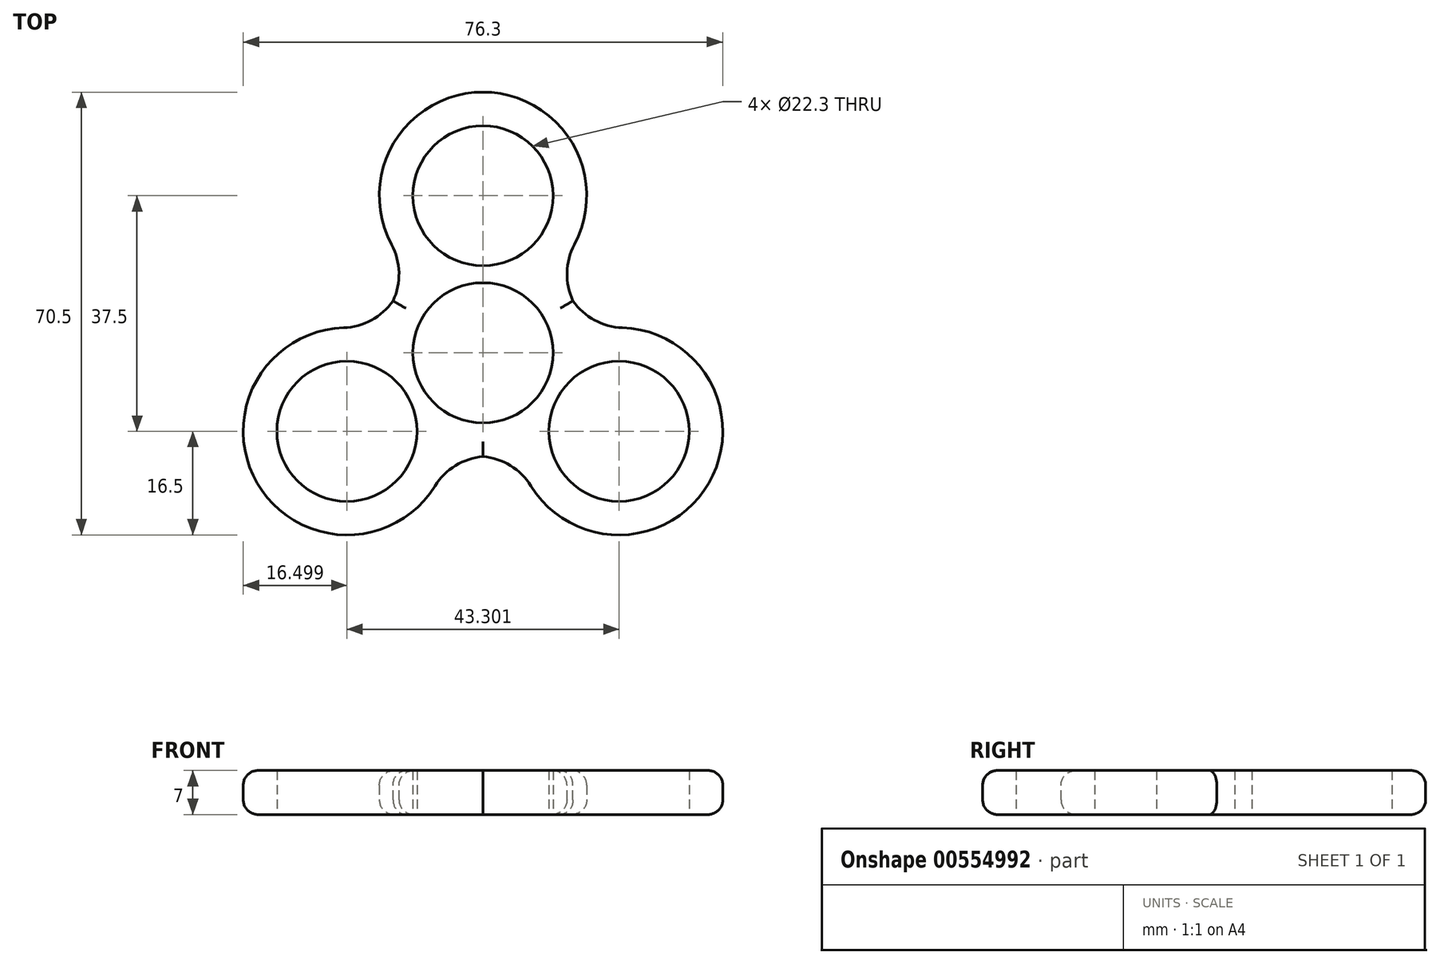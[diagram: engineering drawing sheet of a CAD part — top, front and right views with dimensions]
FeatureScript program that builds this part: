
annotation { "Feature Type Name" : "Feature", "Feature Type Description" : "" }
export const myFeature = defineFeature(function(context is Context, id is Id, definition is map)
    precondition{}
    {
        {
            var Q0;
            Q0=qCreatedBy(makeId("Top.planeOp"),FACE);
            var sketch = newSketch(context, id + "F0", { "sketchPlane" : qUnion([Q0])});
            skCircle(sketch, "E0", {"center": v(0, 0) * mm, "radius": 11.15 * mm});
            skLineSegment(sketch, "E1", {"start": v(0, 0) * mm, "end": v(0, 25) * mm, "construction": true});
            skCircle(sketch, "E2", {"center": v(0, 25) * mm, "radius": 11.15 * mm});
            skCircle(sketch, "E3.1.0", {"center": v(-21.65, -12.5) * mm, "radius": 11.15 * mm});
            skCircle(sketch, "E3.2.0", {"center": v(21.65, -12.5) * mm, "radius": 11.15 * mm});
            skCircle(sketch, "E4", {"center": v(0, 25) * mm, "radius": 16.5 * mm});
            skCircle(sketch, "E5", {"center": v(21.65, -12.5) * mm, "radius": 16.5 * mm});
            skCircle(sketch, "E6", {"center": v(-21.65, -12.5) * mm, "radius": 16.5 * mm});
            skLineSegment(sketch, "E7", {"start": v(0, 0) * mm, "end": v(-21.65, -12.5) * mm});
            skCircle(sketch, "E8", {"center": v(0, 0) * mm, "radius": 16.5 * mm});
            skSolve(sketch);
        }
        {
            var Q0;
            Q0=qSketchRegion(id+"F0",true);
            extrude(context, id + "F1", {"entities" : qUnion([Q0]), "depth" : 7 * mm, "offsetDistance" : 25 * mm});
        }
        {
            var Q0;
            {var subQ0=sQuery(id+"F0.wireOp",EDGE,"E8");var subQ1=sQuery(id+"F0.wireOp",EDGE,"E6");Q0=makeQuery(id+"F1.opExtrude","SWEPT_EDGE",EDGE,{"disambiguationData":[OSD([subQ1,subQ0]),TDD([makeQuery(id+"F0.imprint","INTERSECT",VERTEX,{"disambiguationData":[OD(1.0)],"derivedFrom":[subQ1,subQ0]})])]});}
            var Q1;
            {var subQ0=sQuery(id+"F0.wireOp",EDGE,"E8");var subQ1=sQuery(id+"F0.wireOp",EDGE,"E4");Q1=makeQuery(id+"F1.opExtrude","SWEPT_EDGE",EDGE,{"disambiguationData":[OSD([subQ1,subQ0]),TDD([makeQuery(id+"F0.imprint","INTERSECT",VERTEX,{"disambiguationData":[OD(0.0)],"derivedFrom":[subQ1,subQ0]})])]});}
            var Q2;
            {var subQ0=sQuery(id+"F0.wireOp",EDGE,"E8");var subQ1=sQuery(id+"F0.wireOp",EDGE,"E4");Q2=makeQuery(id+"F1.opExtrude","SWEPT_EDGE",EDGE,{"disambiguationData":[OSD([subQ1,subQ0]),TDD([makeQuery(id+"F0.imprint","INTERSECT",VERTEX,{"disambiguationData":[OD(1.0)],"derivedFrom":[subQ1,subQ0]})])]});}
            var Q3;
            {var subQ0=sQuery(id+"F0.wireOp",EDGE,"E8");var subQ1=sQuery(id+"F0.wireOp",EDGE,"E5");Q3=makeQuery(id+"F1.opExtrude","SWEPT_EDGE",EDGE,{"disambiguationData":[OSD([subQ1,subQ0]),TDD([makeQuery(id+"F0.imprint","INTERSECT",VERTEX,{"disambiguationData":[OD(1.0)],"derivedFrom":[subQ1,subQ0]})])]});}
            var Q4;
            {var subQ0=sQuery(id+"F0.wireOp",EDGE,"E8");var subQ1=sQuery(id+"F0.wireOp",EDGE,"E5");Q4=makeQuery(id+"F1.opExtrude","SWEPT_EDGE",EDGE,{"disambiguationData":[OSD([subQ1,subQ0]),TDD([makeQuery(id+"F0.imprint","INTERSECT",VERTEX,{"disambiguationData":[OD(0.0)],"derivedFrom":[subQ1,subQ0]})])]});}
            var Q5;
            {var subQ0=sQuery(id+"F0.wireOp",EDGE,"E8");var subQ1=sQuery(id+"F0.wireOp",EDGE,"E6");Q5=makeQuery(id+"F1.opExtrude","SWEPT_EDGE",EDGE,{"disambiguationData":[OSD([subQ1,subQ0]),TDD([makeQuery(id+"F0.imprint","INTERSECT",VERTEX,{"disambiguationData":[OD(0.0)],"derivedFrom":[subQ1,subQ0]})])]});}
            fillet(context, id + "F2", {"entities" : qUnion([Q0, Q1, Q2, Q3, Q4, Q5]), "radius" : 10 * mm, "tangentPropagation" : true, "allowEdgeOverflow" : false});
        }
        {
            var Q0;
            Q0=makeQuery(id+"F1.opExtrude","CAP_EDGE",EDGE,{"disambiguationData":[OSD([sQuery(id+"F0.wireOp",EDGE,"E4")])],"isStart":false});
            var Q1;
            {var subQ0=sQuery(id+"F0.wireOp",EDGE,"E8");var subQ1=sQuery(id+"F0.wireOp",EDGE,"E4");Q1=makeQuery(id+"F2.opFillet","BLEND_EDGE",EDGE,{"blendedFrom":[makeQuery(id+"F1.opExtrude","SWEPT_EDGE",EDGE,{"disambiguationData":[OSD([subQ1,subQ0]),TDD([makeQuery(id+"F0.imprint","INTERSECT",VERTEX,{"disambiguationData":[OD(0.0)],"derivedFrom":[subQ1,subQ0]})])]}),makeQuery(id+"F1.opExtrude","CAP_FACE",FACE,{"disambiguationData":[OSD([sQuery(id+"F0.wireOp",EDGE,"E0"),sQuery(id+"F0.wireOp",EDGE,"E2"),sQuery(id+"F0.wireOp",EDGE,"E3.1.0"),sQuery(id+"F0.wireOp",EDGE,"E3.2.0"),subQ1,sQuery(id+"F0.wireOp",EDGE,"E5"),sQuery(id+"F0.wireOp",EDGE,"E6"),subQ0])],"isStart":false})],"blendedInto":[makeQuery(id+"F1.opExtrude","CAP_FACE",FACE,{"disambiguationData":[OSD([sQuery(id+"F0.wireOp",EDGE,"E0"),sQuery(id+"F0.wireOp",EDGE,"E2"),sQuery(id+"F0.wireOp",EDGE,"E3.1.0"),sQuery(id+"F0.wireOp",EDGE,"E3.2.0"),subQ1,sQuery(id+"F0.wireOp",EDGE,"E5"),sQuery(id+"F0.wireOp",EDGE,"E6"),subQ0])],"isStart":false})]});}
            var Q2;
            {var subQ0=sQuery(id+"F0.wireOp",EDGE,"E8");var subQ1=sQuery(id+"F0.wireOp",EDGE,"E6");Q2=makeQuery(id+"F2.opFillet","BLEND_EDGE",EDGE,{"blendedFrom":[makeQuery(id+"F1.opExtrude","SWEPT_EDGE",EDGE,{"disambiguationData":[OSD([subQ1,subQ0]),TDD([makeQuery(id+"F0.imprint","INTERSECT",VERTEX,{"disambiguationData":[OD(1.0)],"derivedFrom":[subQ1,subQ0]})])]}),makeQuery(id+"F1.opExtrude","CAP_FACE",FACE,{"disambiguationData":[OSD([sQuery(id+"F0.wireOp",EDGE,"E0"),sQuery(id+"F0.wireOp",EDGE,"E2"),sQuery(id+"F0.wireOp",EDGE,"E3.1.0"),sQuery(id+"F0.wireOp",EDGE,"E3.2.0"),sQuery(id+"F0.wireOp",EDGE,"E4"),sQuery(id+"F0.wireOp",EDGE,"E5"),subQ1,subQ0])],"isStart":false})],"blendedInto":[makeQuery(id+"F1.opExtrude","CAP_FACE",FACE,{"disambiguationData":[OSD([sQuery(id+"F0.wireOp",EDGE,"E0"),sQuery(id+"F0.wireOp",EDGE,"E2"),sQuery(id+"F0.wireOp",EDGE,"E3.1.0"),sQuery(id+"F0.wireOp",EDGE,"E3.2.0"),sQuery(id+"F0.wireOp",EDGE,"E4"),sQuery(id+"F0.wireOp",EDGE,"E5"),subQ1,subQ0])],"isStart":false})]});}
            var Q3;
            Q3=makeQuery(id+"F1.opExtrude","CAP_EDGE",EDGE,{"disambiguationData":[OSD([sQuery(id+"F0.wireOp",EDGE,"E6")])],"isStart":false});
            var Q4;
            {var subQ0=sQuery(id+"F0.wireOp",EDGE,"E8");var subQ1=sQuery(id+"F0.wireOp",EDGE,"E5");Q4=makeQuery(id+"F2.opFillet","BLEND_EDGE",EDGE,{"blendedFrom":[makeQuery(id+"F1.opExtrude","SWEPT_EDGE",EDGE,{"disambiguationData":[OSD([subQ1,subQ0]),TDD([makeQuery(id+"F0.imprint","INTERSECT",VERTEX,{"disambiguationData":[OD(0.0)],"derivedFrom":[subQ1,subQ0]})])]}),makeQuery(id+"F1.opExtrude","CAP_FACE",FACE,{"disambiguationData":[OSD([sQuery(id+"F0.wireOp",EDGE,"E0"),sQuery(id+"F0.wireOp",EDGE,"E2"),sQuery(id+"F0.wireOp",EDGE,"E3.1.0"),sQuery(id+"F0.wireOp",EDGE,"E3.2.0"),sQuery(id+"F0.wireOp",EDGE,"E4"),subQ1,sQuery(id+"F0.wireOp",EDGE,"E6"),subQ0])],"isStart":false})],"blendedInto":[makeQuery(id+"F1.opExtrude","CAP_FACE",FACE,{"disambiguationData":[OSD([sQuery(id+"F0.wireOp",EDGE,"E0"),sQuery(id+"F0.wireOp",EDGE,"E2"),sQuery(id+"F0.wireOp",EDGE,"E3.1.0"),sQuery(id+"F0.wireOp",EDGE,"E3.2.0"),sQuery(id+"F0.wireOp",EDGE,"E4"),subQ1,sQuery(id+"F0.wireOp",EDGE,"E6"),subQ0])],"isStart":false})]});}
            var Q5;
            Q5=makeQuery(id+"F1.opExtrude","CAP_EDGE",EDGE,{"disambiguationData":[OSD([sQuery(id+"F0.wireOp",EDGE,"E5")])],"isStart":false});
            var Q6;
            Q6=makeQuery(id+"F1.opExtrude","CAP_EDGE",EDGE,{"disambiguationData":[OSD([sQuery(id+"F0.wireOp",EDGE,"E6")])],"isStart":true});
            var Q7;
            {var subQ0=sQuery(id+"F0.wireOp",EDGE,"E8");var subQ1=sQuery(id+"F0.wireOp",EDGE,"E6");Q7=makeQuery(id+"F2.opFillet","BLEND_EDGE",EDGE,{"blendedFrom":[makeQuery(id+"F1.opExtrude","SWEPT_EDGE",EDGE,{"disambiguationData":[OSD([subQ1,subQ0]),TDD([makeQuery(id+"F0.imprint","INTERSECT",VERTEX,{"disambiguationData":[OD(0.0)],"derivedFrom":[subQ1,subQ0]})])]}),makeQuery(id+"F1.opExtrude","CAP_FACE",FACE,{"disambiguationData":[OSD([sQuery(id+"F0.wireOp",EDGE,"E0"),sQuery(id+"F0.wireOp",EDGE,"E2"),sQuery(id+"F0.wireOp",EDGE,"E3.1.0"),sQuery(id+"F0.wireOp",EDGE,"E3.2.0"),sQuery(id+"F0.wireOp",EDGE,"E4"),sQuery(id+"F0.wireOp",EDGE,"E5"),subQ1,subQ0])],"isStart":true})],"blendedInto":[makeQuery(id+"F1.opExtrude","CAP_FACE",FACE,{"disambiguationData":[OSD([sQuery(id+"F0.wireOp",EDGE,"E0"),sQuery(id+"F0.wireOp",EDGE,"E2"),sQuery(id+"F0.wireOp",EDGE,"E3.1.0"),sQuery(id+"F0.wireOp",EDGE,"E3.2.0"),sQuery(id+"F0.wireOp",EDGE,"E4"),sQuery(id+"F0.wireOp",EDGE,"E5"),subQ1,subQ0])],"isStart":true})]});}
            var Q8;
            Q8=makeQuery(id+"F1.opExtrude","CAP_EDGE",EDGE,{"disambiguationData":[OSD([sQuery(id+"F0.wireOp",EDGE,"E5")])],"isStart":true});
            var Q9;
            {var subQ0=sQuery(id+"F0.wireOp",EDGE,"E8");var subQ1=sQuery(id+"F0.wireOp",EDGE,"E5");Q9=makeQuery(id+"F2.opFillet","BLEND_EDGE",EDGE,{"blendedFrom":[makeQuery(id+"F1.opExtrude","SWEPT_EDGE",EDGE,{"disambiguationData":[OSD([subQ1,subQ0]),TDD([makeQuery(id+"F0.imprint","INTERSECT",VERTEX,{"disambiguationData":[OD(1.0)],"derivedFrom":[subQ1,subQ0]})])]}),makeQuery(id+"F1.opExtrude","CAP_FACE",FACE,{"disambiguationData":[OSD([sQuery(id+"F0.wireOp",EDGE,"E0"),sQuery(id+"F0.wireOp",EDGE,"E2"),sQuery(id+"F0.wireOp",EDGE,"E3.1.0"),sQuery(id+"F0.wireOp",EDGE,"E3.2.0"),sQuery(id+"F0.wireOp",EDGE,"E4"),subQ1,sQuery(id+"F0.wireOp",EDGE,"E6"),subQ0])],"isStart":true})],"blendedInto":[makeQuery(id+"F1.opExtrude","CAP_FACE",FACE,{"disambiguationData":[OSD([sQuery(id+"F0.wireOp",EDGE,"E0"),sQuery(id+"F0.wireOp",EDGE,"E2"),sQuery(id+"F0.wireOp",EDGE,"E3.1.0"),sQuery(id+"F0.wireOp",EDGE,"E3.2.0"),sQuery(id+"F0.wireOp",EDGE,"E4"),subQ1,sQuery(id+"F0.wireOp",EDGE,"E6"),subQ0])],"isStart":true})]});}
            var Q10;
            {var subQ0=sQuery(id+"F0.wireOp",EDGE,"E8");var subQ1=sQuery(id+"F0.wireOp",EDGE,"E4");Q10=makeQuery(id+"F2.opFillet","BLEND_EDGE",EDGE,{"blendedFrom":[makeQuery(id+"F1.opExtrude","SWEPT_EDGE",EDGE,{"disambiguationData":[OSD([subQ1,subQ0]),TDD([makeQuery(id+"F0.imprint","INTERSECT",VERTEX,{"disambiguationData":[OD(1.0)],"derivedFrom":[subQ1,subQ0]})])]}),makeQuery(id+"F1.opExtrude","CAP_FACE",FACE,{"disambiguationData":[OSD([sQuery(id+"F0.wireOp",EDGE,"E0"),sQuery(id+"F0.wireOp",EDGE,"E2"),sQuery(id+"F0.wireOp",EDGE,"E3.1.0"),sQuery(id+"F0.wireOp",EDGE,"E3.2.0"),subQ1,sQuery(id+"F0.wireOp",EDGE,"E5"),sQuery(id+"F0.wireOp",EDGE,"E6"),subQ0])],"isStart":true})],"blendedInto":[makeQuery(id+"F1.opExtrude","CAP_FACE",FACE,{"disambiguationData":[OSD([sQuery(id+"F0.wireOp",EDGE,"E0"),sQuery(id+"F0.wireOp",EDGE,"E2"),sQuery(id+"F0.wireOp",EDGE,"E3.1.0"),sQuery(id+"F0.wireOp",EDGE,"E3.2.0"),subQ1,sQuery(id+"F0.wireOp",EDGE,"E5"),sQuery(id+"F0.wireOp",EDGE,"E6"),subQ0])],"isStart":true})]});}
            var Q11;
            Q11=makeQuery(id+"F1.opExtrude","CAP_EDGE",EDGE,{"disambiguationData":[OSD([sQuery(id+"F0.wireOp",EDGE,"E4")])],"isStart":true});
            fillet(context, id + "F3", {"entities" : qUnion([Q0, Q1, Q2, Q3, Q4, Q5, Q6, Q7, Q8, Q9, Q10, Q11]), "radius" : 2.33 * mm, "tangentPropagation" : true, "allowEdgeOverflow" : false});
        }
    });
